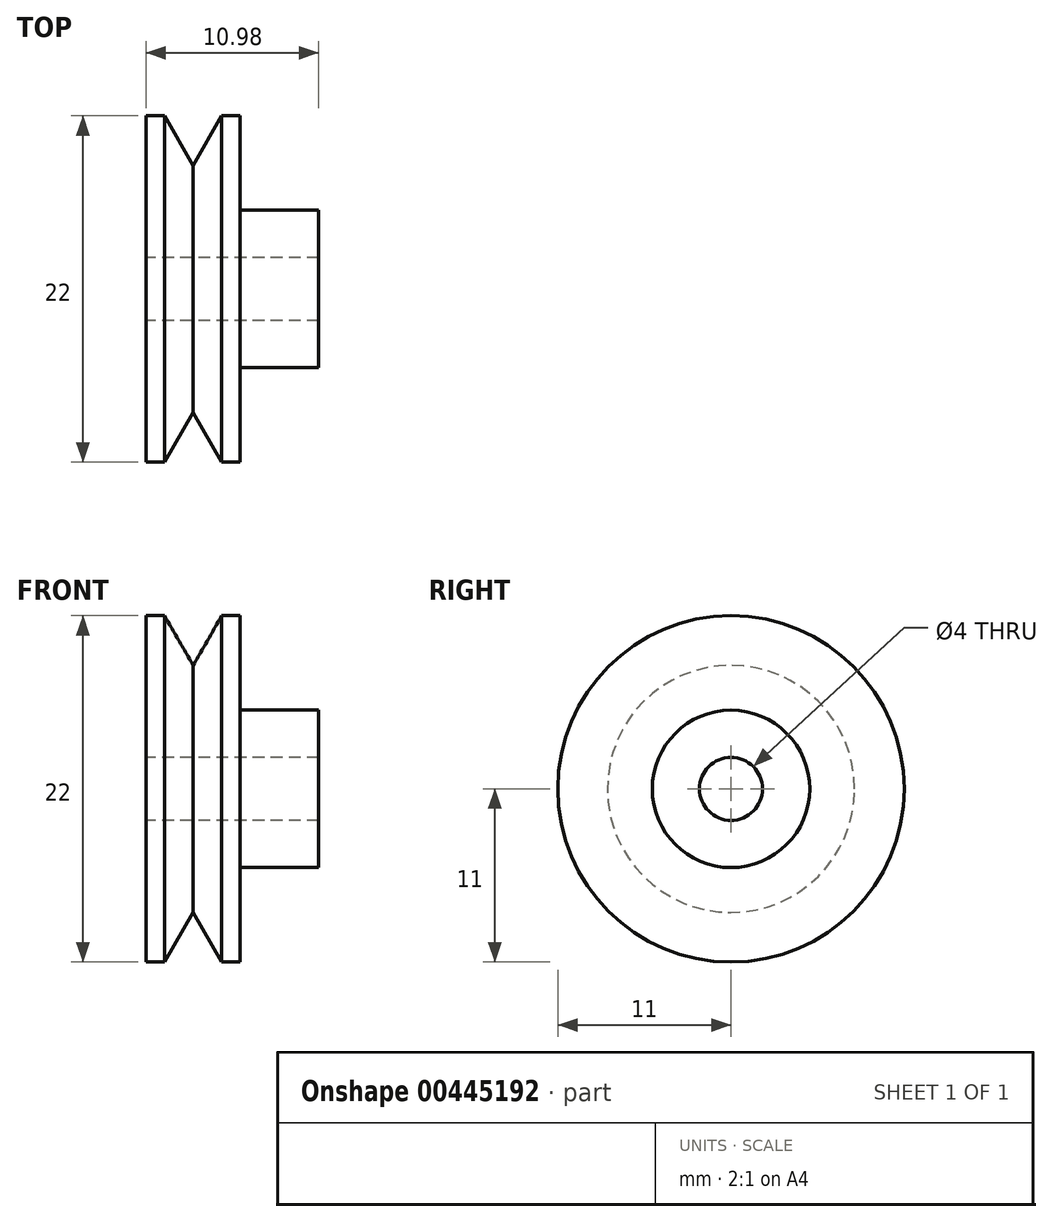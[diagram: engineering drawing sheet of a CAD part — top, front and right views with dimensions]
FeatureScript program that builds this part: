
annotation { "Feature Type Name" : "Feature", "Feature Type Description" : "" }
export const myFeature = defineFeature(function(context is Context, id is Id, definition is map)
    precondition{}
    {
        {
            var Q0;
            Q0=qCreatedBy(makeId("Front.planeOp"),FACE);
            var sketch = newSketch(context, id + "F0", { "sketchPlane" : qUnion([Q0])});
            skLineSegment(sketch, "E0", {"start": v(-53.82, 0) * mm, "end": v(43.6, 0) * mm, "construction": true});
            skLineSegment(sketch, "E1", {"start": v(-3, 2) * mm, "end": v(7.98, 2) * mm});
            skLineSegment(sketch, "E2", {"start": v(-3, 11) * mm, "end": v(-1.82, 11) * mm});
            skLineSegment(sketch, "E3.0", {"start": v(-3, 2) * mm, "end": v(-3, 11) * mm});
            skLineSegment(sketch, "E4.0", {"start": v(3, 5) * mm, "end": v(3, 11) * mm});
            skLineSegment(sketch, "E5.0", {"start": v(2.98, 5) * mm, "end": v(2.98, 11) * mm});
            skLineSegment(sketch, "E6.0", {"start": v(7.98, 2) * mm, "end": v(7.98, 5) * mm});
            skLineSegment(sketch, "E7.trimOffspring", {"start": v(2.98, 5) * mm, "end": v(7.98, 5) * mm});
            skLineSegment(sketch, "E8", {"start": v(0, 7.85) * mm, "end": v(1.82, 11) * mm});
            skLineSegment(sketch, "E9.MirrorCS", {"start": v(0, 7.85) * mm, "end": v(-1.82, 11) * mm});
            skLineSegment(sketch, "E10.trimOffspring", {"start": v(1.82, 11) * mm, "end": v(3, 11) * mm});
            skSolve(sketch);
        }
        {
            var Q0;
            Q0=makeQuery(id+"F0.imprint","IMPRINT",FACE,{"disambiguationData":[TD([[makeQuery(id+"F0.imprint","IMPRINT",EDGE,{"derivedFrom":sQuery(id+"F0.wireOp",EDGE,"E1")}),1.0]])]});
            var Q1;
            Q1=sQuery(id+"F0.wireOp",EDGE,"E0");
            revolve(context, id + "F1", {"entities" : qUnion([Q0]), "axis" : qUnion([Q1]), "revolveType" : RevolveType.FULL});
        }
    });
